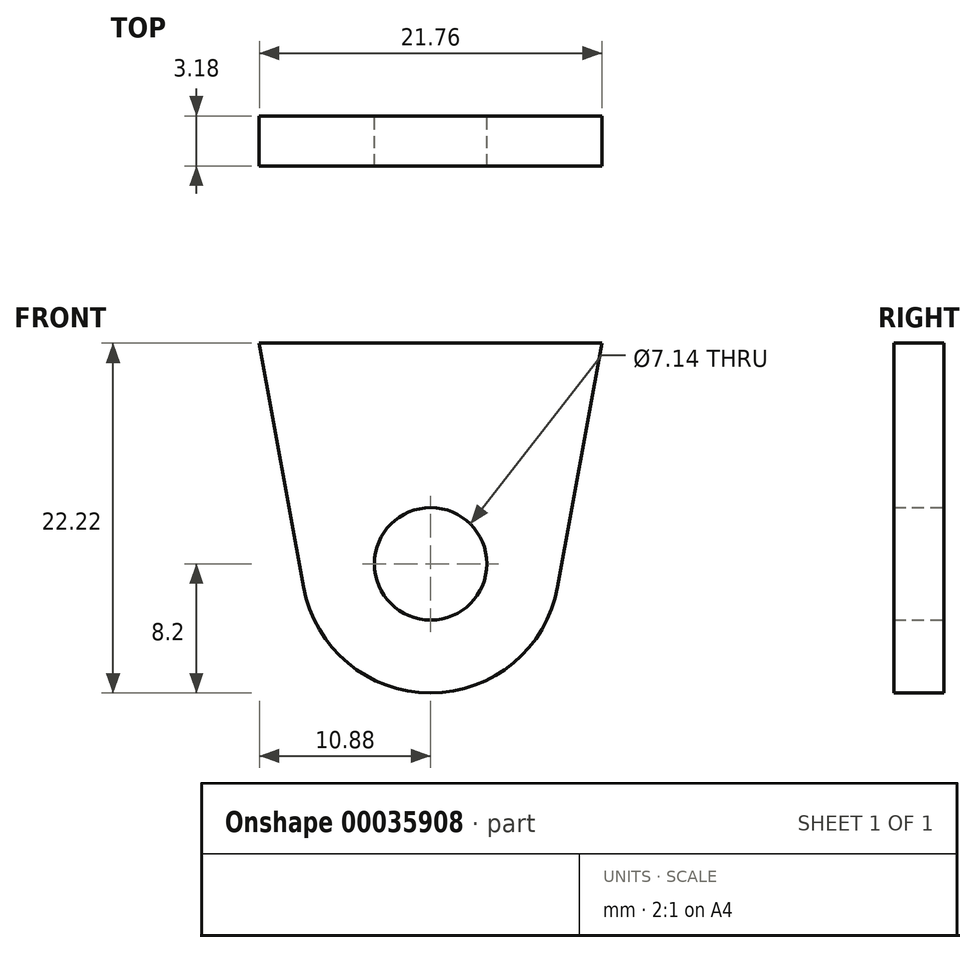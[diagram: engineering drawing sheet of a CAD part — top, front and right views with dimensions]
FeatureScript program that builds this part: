
annotation { "Feature Type Name" : "Feature", "Feature Type Description" : "" }
export const myFeature = defineFeature(function(context is Context, id is Id, definition is map)
    precondition{}
    {
        {
            var Q0;
            Q0=qCreatedBy(makeId("Front.planeOp"),FACE);
            var sketch = newSketch(context, id + "F0", { "sketchPlane" : qUnion([Q0])});
            skCircle(sketch, "E0", {"center": v(0, 0) * mm, "radius": 3.57 * mm});
            skArc(sketch, "E1", {"start": v(-8.07, -1.47) * mm, "mid": v(0, -8.2) * mm, "end": v(8.07, -1.47) * mm});
            skLineSegment(sketch, "E2", {"start": v(-10.88, 14.02) * mm, "end": v(10.88, 14.02) * mm});
            skLineSegment(sketch, "E3", {"start": v(10.88, 14.02) * mm, "end": v(8.07, -1.47) * mm});
            skLineSegment(sketch, "E4", {"start": v(-10.88, 14.02) * mm, "end": v(-8.07, -1.47) * mm});
            skSolve(sketch);
        }
        {
            var Q0;
            Q0=makeQuery(id+"F0.imprint","IMPRINT",FACE,{"disambiguationData":[TD([[makeQuery(id+"F0.imprint","IMPRINT",EDGE,{"derivedFrom":sQuery(id+"F0.wireOp",EDGE,"E0")}),-1.0]])]});
            extrude(context, id + "F1", {"entities" : qUnion([Q0]), "depth" : 3.17 * mm, "symmetric" : true});
        }
    });
